# Revit family: Aquatica_True_Ofuro_Nano
name_source: partatom
category: Plumbing Fixtures
revit_build: Autodesk Revit 2018 (Build: 20170223_1515(x64)
units: mm (PartAtom-declared; Revit-internal decimal feet)

## family parameters
Always vertical = Yes
Cut with Voids When Loaded = No
OmniClass Number = 23.45.00.00
OmniClass Title = Sanitary, Laundry, and Cleaning Equipment
Part Type = Normal
Room Calculation Point = No
Round Connector Dimension = Use Diameter
Shared = No
Work Plane-Based = No

## types (2) — shared parameters
Assembly required = Reversible
Country where manufactured = EU
Current = 16 A
Depth to overflow drain (cm) = 61,3
Description = Aquatica introduces the True Ofuro Nano, the ultimate micro tub for small spaces. Increasing demand for narrow bathtubs inspired Aquatica’s international design team to create a slimmer version of the best selling Japanese inspired True Ofuro soaking tub.

The tub’s oval, slender design ensures easy access through narrow passageways and doorways, making it the perfect tub for all types of buildings. Made of award-winning, lightweight stone composite AquateX™, the True Ofuro Nano is easy to transport and install in any bathroom.

Despite its tiny size, this modern adaptation of the traditional soaker provides ultimate comfort with an ergonomically designed built-in seat, and an integrated backrest with neck support. The Nano’s impressive depth allows the bather to fully submerge, and enjoy a truly tranquil soak.
Drain placement = Center
Exterior dimensions (cm) = 123,7 L x 78,9 W x 93,7 H
Installation type = Freestanding
Interior dimensions (cm) = 111 L x 69,5 W x 67,8 H
Load classification = Power
Manufacturer = Aquatica
Model = True Ofuro
Shape = Oval
Surface finish = Matte
URL = https://www.aquaticabath.eu
Voltage = 220 V
Warranty = 25 Year Limited Warranty

## per-type parameters (varying)
| type | Apparent Power | Product Material | Product color | Product material |
| Color - (White) Size - (123,7x78,9x93,7 cm) | 2500 VA | Aquatica-Ceramics-White | White | AquateX™ |
| Color - (Black) Size - (123,7x78,9x93,7 cm) | 0 VA | Aquatica-Ceramics-Black grey | Black | NeroX™ |

## geometry (parser evidence)
native form markers: Sweep x4
no freeform markers — native parametric forms only
